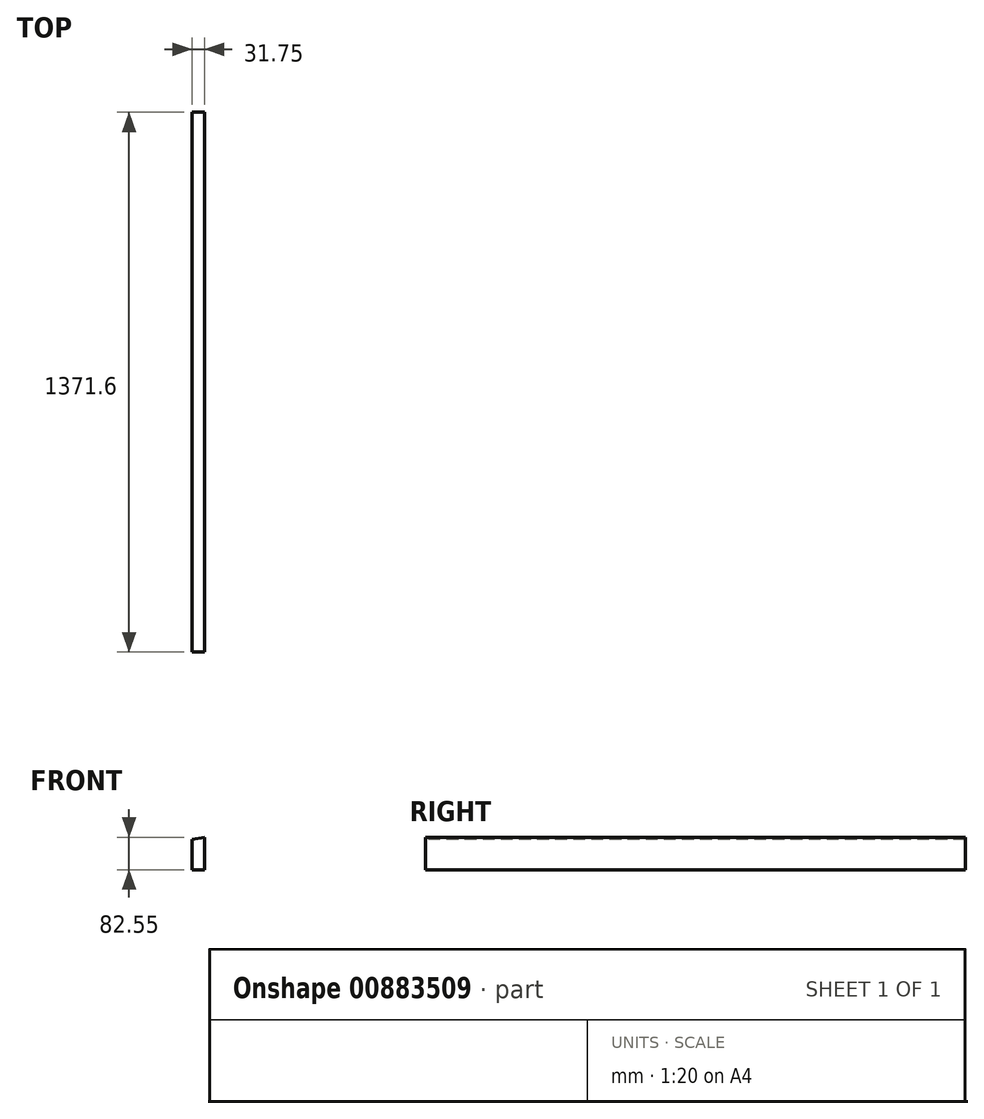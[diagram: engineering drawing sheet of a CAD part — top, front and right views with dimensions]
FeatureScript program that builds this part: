
annotation { "Feature Type Name" : "Feature", "Feature Type Description" : "" }
export const myFeature = defineFeature(function(context is Context, id is Id, definition is map)
    precondition{}
    {
        {
            var Q0;
            Q0=qCreatedBy(makeId("Front.planeOp"),FACE);
            var sketch = newSketch(context, id + "F0", { "sketchPlane" : qUnion([Q0])});
            skLineSegment(sketch, "E0.bottom", {"start": v(0, 0) * mm, "end": v(31.75, 0) * mm});
            skLineSegment(sketch, "E0.top", {"start": v(0, 82.55) * mm, "end": v(31.75, 82.55) * mm, "construction": true});
            skLineSegment(sketch, "E0.left", {"start": v(0, 0) * mm, "end": v(0, 76.95) * mm});
            skLineSegment(sketch, "E0.right", {"start": v(31.75, 0) * mm, "end": v(31.75, 82.55) * mm});
            skLineSegment(sketch, "E1", {"start": v(31.75, 82.55) * mm, "end": v(0, 76.95) * mm});
            skLineSegment(sketch, "E2", {"start": v(0, 76.95) * mm, "end": v(0, 82.55) * mm, "construction": true});
            skSolve(sketch);
        }
        {
            var Q0;
            Q0=qSketchRegion(id+"F0",true);
            extrude(context, id + "F1", {"entities" : qUnion([Q0]), "oppositeDirection" : true, "depth" : 1371.6 * mm, "offsetDistance" : 25.4 * mm});
        }
    });
